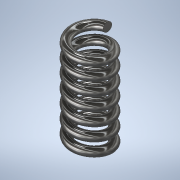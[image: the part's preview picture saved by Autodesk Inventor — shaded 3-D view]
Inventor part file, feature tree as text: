
AUTODESK INVENTOR PART (.ipt)
format: ipt  version: 2021 (Build 250183000, 183)  size: 324,096 bytes
history: native  units: in
note: dims shown in document units (in); Inventor stores cm internally (conversion verified against a paired STEP export)
features: helix x1, sketch x1
ambient origin geometry x8: Origin, YZ Plane, XZ Plane, XY Plane, X Axis, Y Axis, Z Axis, Center Point
bodies: Solid1 (feature_tree)
feature tree (2):
  helix  "Coil1"  [1 undecoded]
  sketch  "Sketch1"  dims[d1=0.0039in d2=0.1205in d3=0.0059in d4=1.0in d5=2.7559in d6=0.0in d7=90.0deg d8=90.0deg d9=0.0in d10=0.0in]
note: 1 required parameter value undecoded (feature->parameter linkage not recoverable at this tier; creation-order binding heuristic only, values carry confidence <= 0.55)
